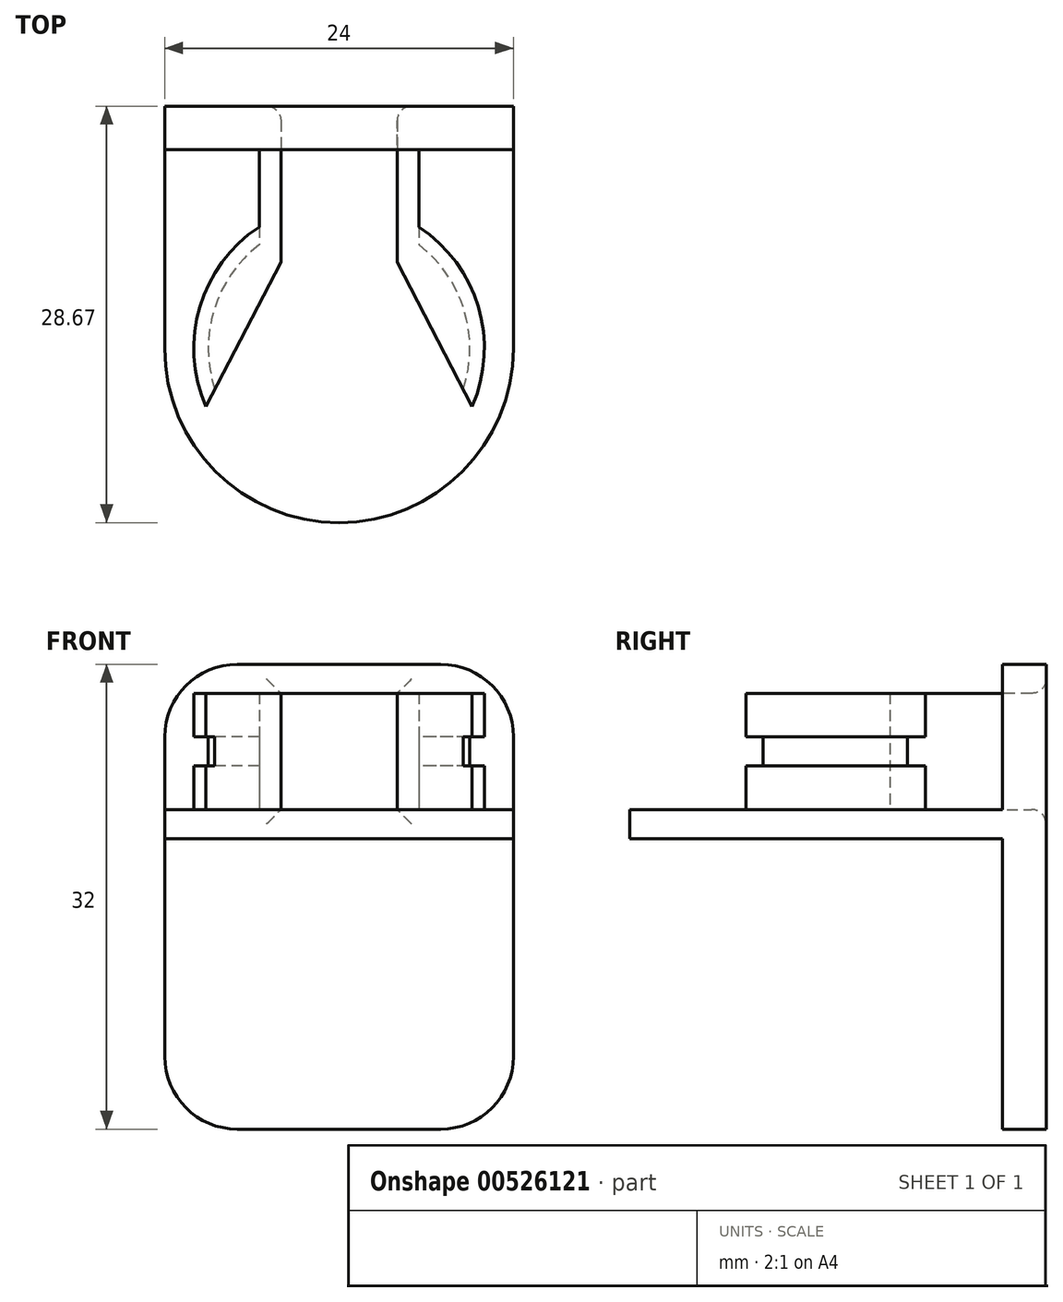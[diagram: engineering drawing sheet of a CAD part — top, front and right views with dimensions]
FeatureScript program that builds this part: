
annotation { "Feature Type Name" : "Feature", "Feature Type Description" : "" }
export const myFeature = defineFeature(function(context is Context, id is Id, definition is map)
    precondition{}
    {
        {
            var Q0;
            Q0=qCreatedBy(makeId("Top.planeOp"),FACE);
            var sketch = newSketch(context, id + "F0", { "sketchPlane" : qUnion([Q0])});
            skArc(sketch, "E0", {"start": v(-5.5, 1.5) * mm, "mid": v(0, 24.17) * mm, "end": v(5.5, 1.5) * mm});
            skArc(sketch, "E1", {"start": v(-5.5, -1.5) * mm, "mid": v(0, -24.17) * mm, "end": v(5.5, -1.5) * mm});
            skLineSegment(sketch, "E2", {"start": v(-5.5, 1.5) * mm, "end": v(-5.5, -1.5) * mm});
            skLineSegment(sketch, "E3", {"start": v(5.5, 1.5) * mm, "end": v(5.5, -1.5) * mm});
            skSolve(sketch);
        }
        {
            var Q0;
            Q0=qSketchRegion(id+"F0",true);
            extrude(context, id + "F1", {"entities" : qUnion([Q0]), "depth" : 2 * mm, "offsetDistance" : 25 * mm});
        }
        {
            var Q0;
            Q0=makeQuery(id+"F1.opExtrude","CAP_FACE",FACE,{"disambiguationData":[OSD([sQuery(id+"F0.wireOp",EDGE,"E0"),sQuery(id+"F0.wireOp",EDGE,"E1"),sQuery(id+"F0.wireOp",EDGE,"E2"),sQuery(id+"F0.wireOp",EDGE,"E3")])],"isStart":false});
            var sketch = newSketch(context, id + "F2", { "sketchPlane" : qUnion([Q0])});
            skArc(sketch, "E4", {"start": v(8.66, 17.17) * mm, "mid": v(9.5, 9.04) * mm, "end": v(4, 3) * mm});
            skArc(sketch, "E5", {"start": v(9.78, 19.11) * mm, "mid": v(11.66, 9.33) * mm, "end": v(5.5, 1.5) * mm});
            skArc(sketch, "E6", {"start": v(-8.66, 17.17) * mm, "mid": v(-9.5, 9.04) * mm, "end": v(-4, 3) * mm});
            skArc(sketch, "E7", {"start": v(5.5, -3.81) * mm, "mid": v(9.59, -9.32) * mm, "end": v(9.17, -16.17) * mm});
            skLineSegment(sketch, "E8", {"start": v(9.78, 19.11) * mm, "end": v(8.66, 17.17) * mm});
            skLineSegment(sketch, "E9", {"start": v(-8.66, 17.17) * mm, "end": v(-9.78, 19.11) * mm});
            skLineSegment(sketch, "E10", {"start": v(5.5, 1.5) * mm, "end": v(5.5, -3.81) * mm});
            skLineSegment(sketch, "E11", {"start": v(-4, 3) * mm, "end": v(-4, -6.24) * mm});
            skLineSegment(sketch, "E12", {"start": v(-4, -6.24) * mm, "end": v(-9.17, -16.17) * mm});
            skLineSegment(sketch, "E13", {"start": v(9.17, -16.17) * mm, "end": v(4, -6.24) * mm});
            skLineSegment(sketch, "E14", {"start": v(4, -6.24) * mm, "end": v(4, 3) * mm});
            skArc(sketch, "E15", {"start": v(-9.78, 19.11) * mm, "mid": v(-11.66, 9.33) * mm, "end": v(-5.5, 1.5) * mm});
            skArc(sketch, "E16", {"start": v(-9.17, -16.17) * mm, "mid": v(-9.59, -9.32) * mm, "end": v(-5.5, -3.81) * mm});
            skLineSegment(sketch, "E17", {"start": v(-5.5, 1.5) * mm, "end": v(-5.5, -3.81) * mm});
            skArc(sketch, "E18.0", {"start": v(-5.5, 1.5) * mm, "mid": v(0, 24.17) * mm, "end": v(5.5, 1.5) * mm, "construction": true});
            skArc(sketch, "E19.0", {"start": v(-5.5, -1.5) * mm, "mid": v(0, -24.17) * mm, "end": v(5.5, -1.5) * mm, "construction": true});
            skSolve(sketch);
        }
        {
            var Q0;
            Q0=qSketchRegion(id+"F2",true);
            extrude(context, id + "F3", {"entities" : qUnion([Q0]), "operationType" : NewBodyOperationType.ADD, "depth" : 3 * mm, "offsetDistance" : 25 * mm});
        }
        {
            var Q0;
            Q0=makeQuery(id+"F3.opExtrude","CAP_FACE",FACE,{"disambiguationData":[OSD([sQuery(id+"F2.wireOp",EDGE,"E4"),sQuery(id+"F2.wireOp",EDGE,"E5"),sQuery(id+"F2.wireOp",EDGE,"E7"),sQuery(id+"F2.wireOp",EDGE,"E8"),sQuery(id+"F2.wireOp",EDGE,"E10"),sQuery(id+"F2.wireOp",EDGE,"E13"),sQuery(id+"F2.wireOp",EDGE,"E14")])],"isStart":false});
            var sketch = newSketch(context, id + "F4", { "sketchPlane" : qUnion([Q0])});
            skArc(sketch, "E20", {"start": v(-9.78, 19.11) * mm, "mid": v(-11.66, 9.33) * mm, "end": v(-5.5, 1.5) * mm});
            skArc(sketch, "E21", {"start": v(9.78, 19.11) * mm, "mid": v(11.66, 9.33) * mm, "end": v(5.5, 1.5) * mm});
            skArc(sketch, "E22", {"start": v(8.07, 16.15) * mm, "mid": v(8.53, 9.28) * mm, "end": v(4, 4.1) * mm});
            skArc(sketch, "E23", {"start": v(-8.07, 16.15) * mm, "mid": v(-8.53, 9.28) * mm, "end": v(-4, 4.1) * mm});
            skArc(sketch, "E24", {"start": v(5.5, -5.04) * mm, "mid": v(8.6, -9.53) * mm, "end": v(8.55, -14.98) * mm});
            skArc(sketch, "E25", {"start": v(-5.5, -5.04) * mm, "mid": v(-8.6, -9.53) * mm, "end": v(-8.55, -14.98) * mm});
            skLineSegment(sketch, "E26", {"start": v(-5.5, 1.5) * mm, "end": v(-5.5, -5.04) * mm});
            skLineSegment(sketch, "E27", {"start": v(5.5, 1.5) * mm, "end": v(5.5, -5.04) * mm});
            skLineSegment(sketch, "E28", {"start": v(-4, 4.1) * mm, "end": v(-4, -6.24) * mm});
            skLineSegment(sketch, "E29", {"start": v(-4, -6.24) * mm, "end": v(-8.55, -14.98) * mm});
            skLineSegment(sketch, "E30", {"start": v(4, 4.1) * mm, "end": v(4, -6.24) * mm});
            skLineSegment(sketch, "E31", {"start": v(4, -6.24) * mm, "end": v(8.55, -14.98) * mm});
            skLineSegment(sketch, "E32", {"start": v(8.07, 16.15) * mm, "end": v(9.78, 19.11) * mm});
            skLineSegment(sketch, "E33", {"start": v(-9.78, 19.11) * mm, "end": v(-8.07, 16.15) * mm});
            skLineSegment(sketch, "E34.0", {"start": v(-8.66, 17.17) * mm, "end": v(-9.78, 19.11) * mm, "construction": true});
            skLineSegment(sketch, "E35.0", {"start": v(9.78, 19.11) * mm, "end": v(8.66, 17.17) * mm, "construction": true});
            skLineSegment(sketch, "E36.0", {"start": v(-4, -6.24) * mm, "end": v(-9.17, -16.17) * mm, "construction": true});
            skLineSegment(sketch, "E37.0", {"start": v(9.17, -16.17) * mm, "end": v(4, -6.24) * mm, "construction": true});
            skArc(sketch, "E38.0", {"start": v(-9.78, 19.11) * mm, "mid": v(0, 24.17) * mm, "end": v(9.78, 19.11) * mm, "construction": true});
            skArc(sketch, "E39.0", {"start": v(-5.5, -1.5) * mm, "mid": v(0, -24.17) * mm, "end": v(5.5, -1.5) * mm, "construction": true});
            skSolve(sketch);
        }
        {
            var Q0;
            Q0=qSketchRegion(id+"F4",true);
            extrude(context, id + "F5", {"entities" : qUnion([Q0]), "operationType" : NewBodyOperationType.ADD, "depth" : 2 * mm, "offsetDistance" : 25 * mm});
        }
        {
            var Q0;
            Q0=makeQuery(id+"F5.opExtrude","CAP_FACE",FACE,{"disambiguationData":[OSD([sQuery(id+"F4.wireOp",EDGE,"E21"),sQuery(id+"F4.wireOp",EDGE,"E22"),sQuery(id+"F4.wireOp",EDGE,"E24"),sQuery(id+"F4.wireOp",EDGE,"E27"),sQuery(id+"F4.wireOp",EDGE,"E30"),sQuery(id+"F4.wireOp",EDGE,"E31"),sQuery(id+"F4.wireOp",EDGE,"E32")])],"isStart":false});
            var sketch = newSketch(context, id + "F6", { "sketchPlane" : qUnion([Q0])});
            skArc(sketch, "E40", {"start": v(8.66, 17.17) * mm, "mid": v(9.5, 9.04) * mm, "end": v(4, 3) * mm});
            skArc(sketch, "E41", {"start": v(9.78, 19.11) * mm, "mid": v(11.66, 9.33) * mm, "end": v(5.5, 1.5) * mm});
            skArc(sketch, "E42", {"start": v(-8.66, 17.17) * mm, "mid": v(-9.5, 9.04) * mm, "end": v(-4, 3) * mm});
            skArc(sketch, "E43", {"start": v(5.5, -3.81) * mm, "mid": v(9.59, -9.32) * mm, "end": v(9.17, -16.17) * mm});
            skLineSegment(sketch, "E44", {"start": v(9.78, 19.11) * mm, "end": v(8.66, 17.17) * mm});
            skLineSegment(sketch, "E45", {"start": v(-8.66, 17.17) * mm, "end": v(-9.78, 19.11) * mm});
            skLineSegment(sketch, "E46", {"start": v(5.5, 1.5) * mm, "end": v(5.5, -3.81) * mm});
            skLineSegment(sketch, "E47", {"start": v(-4, 3) * mm, "end": v(-4, -6.24) * mm});
            skLineSegment(sketch, "E48", {"start": v(-4, -6.24) * mm, "end": v(-9.17, -16.17) * mm});
            skLineSegment(sketch, "E49", {"start": v(9.17, -16.17) * mm, "end": v(4, -6.24) * mm});
            skLineSegment(sketch, "E50", {"start": v(4, -6.24) * mm, "end": v(4, 3) * mm});
            skArc(sketch, "E51", {"start": v(-9.78, 19.11) * mm, "mid": v(-11.66, 9.33) * mm, "end": v(-5.5, 1.5) * mm});
            skArc(sketch, "E52", {"start": v(-9.17, -16.17) * mm, "mid": v(-9.59, -9.32) * mm, "end": v(-5.5, -3.81) * mm});
            skLineSegment(sketch, "E53", {"start": v(-5.5, 1.5) * mm, "end": v(-5.5, -3.81) * mm});
            skArc(sketch, "E54.0", {"start": v(-5.5, -1.5) * mm, "mid": v(0, -24.17) * mm, "end": v(5.5, -1.5) * mm, "construction": true});
            skArc(sketch, "E55.0", {"start": v(-9.78, 19.11) * mm, "mid": v(0, 24.17) * mm, "end": v(9.78, 19.11) * mm, "construction": true});
            skSolve(sketch);
        }
        {
            var Q0;
            Q0=qSketchRegion(id+"F6",true);
            extrude(context, id + "F7", {"entities" : qUnion([Q0]), "operationType" : NewBodyOperationType.ADD, "depth" : 3 * mm, "offsetDistance" : 25 * mm});
        }
        {
            var Q0;
            Q0=makeQuery(id+"F5.opExtrude","CAP_EDGE",EDGE,{"disambiguationData":[OSD([sQuery(id+"F4.wireOp",EDGE,"E22")])],"isStart":false});
            var Q1;
            Q1=makeQuery(id+"F5.opExtrude","CAP_EDGE",EDGE,{"disambiguationData":[OSD([sQuery(id+"F4.wireOp",EDGE,"E23")])],"isStart":false});
            var Q2;
            Q2=makeQuery(id+"F5.opExtrude","CAP_EDGE",EDGE,{"disambiguationData":[OSD([sQuery(id+"F4.wireOp",EDGE,"E23")])],"isStart":true});
            var Q3;
            Q3=makeQuery(id+"F5.opExtrude","CAP_EDGE",EDGE,{"disambiguationData":[OSD([sQuery(id+"F4.wireOp",EDGE,"E22")])],"isStart":true});
            var Q4;
            Q4=makeQuery(id+"F5.opExtrude","CAP_EDGE",EDGE,{"disambiguationData":[OSD([sQuery(id+"F4.wireOp",EDGE,"E25")])],"isStart":true});
            var Q5;
            Q5=makeQuery(id+"F5.opExtrude","CAP_EDGE",EDGE,{"disambiguationData":[OSD([sQuery(id+"F4.wireOp",EDGE,"E25")])],"isStart":false});
            var Q6;
            Q6=makeQuery(id+"F5.opExtrude","CAP_EDGE",EDGE,{"disambiguationData":[OSD([sQuery(id+"F4.wireOp",EDGE,"E24")])],"isStart":false});
            var Q7;
            Q7=makeQuery(id+"F5.opExtrude","CAP_EDGE",EDGE,{"disambiguationData":[OSD([sQuery(id+"F4.wireOp",EDGE,"E24")])],"isStart":true});
            fillet(context, id + "F8", {"entities" : qUnion([Q0, Q1, Q2, Q3, Q4, Q5, Q6, Q7]), "radius" : 1 * mm, "tangentPropagation" : true, "allowEdgeOverflow" : false});
        }
        {
            var Q0;
            Q0=makeQuery(id+"F7.opExtrude","CAP_FACE",FACE,{"disambiguationData":[OSD([sQuery(id+"F6.wireOp",EDGE,"E40"),sQuery(id+"F6.wireOp",EDGE,"E41"),sQuery(id+"F6.wireOp",EDGE,"E43"),sQuery(id+"F6.wireOp",EDGE,"E44"),sQuery(id+"F6.wireOp",EDGE,"E46"),sQuery(id+"F6.wireOp",EDGE,"E49"),sQuery(id+"F6.wireOp",EDGE,"E50")])],"isStart":false});
            var sketch = newSketch(context, id + "F9", { "sketchPlane" : qUnion([Q0])});
            skLineSegment(sketch, "E56.bottom", {"start": v(-12, 1.5) * mm, "end": v(12, 1.5) * mm});
            skLineSegment(sketch, "E56.top", {"start": v(-12, 24.17) * mm, "end": v(12, 24.17) * mm});
            skLineSegment(sketch, "E56.left", {"start": v(-12, 24.17) * mm, "end": v(-12, 1.5) * mm});
            skLineSegment(sketch, "E56.right", {"start": v(12, 24.17) * mm, "end": v(12, 1.5) * mm});
            skSolve(sketch);
        }
        {
            var Q0;
            Q0=qSketchRegion(id+"F9",true);
            extrude(context, id + "F10", {"entities" : qUnion([Q0]), "operationType" : NewBodyOperationType.REMOVE, "oppositeDirection" : true, "depth" : 10 * mm, "offsetDistance" : 25 * mm});
        }
        {
            var Q0;
            Q0=makeQuery(id+"F10.boolean.opBoolean","COPY",FACE,{"derivedFrom":makeQuery(id+"F10.opExtrude","SWEPT_FACE",FACE,{"disambiguationData":[OSD([sQuery(id+"F9.wireOp",EDGE,"E56.bottom")])]})});
            var sketch = newSketch(context, id + "F11", { "sketchPlane" : qUnion([Q0])});
            skLineSegment(sketch, "E57.bottom", {"start": v(-12, -20) * mm, "end": v(12, -20) * mm});
            skLineSegment(sketch, "E57.top", {"start": v(-12, 12) * mm, "end": v(12, 12) * mm});
            skLineSegment(sketch, "E57.left", {"start": v(-12, 12) * mm, "end": v(-12, -20) * mm});
            skLineSegment(sketch, "E57.right", {"start": v(12, 12) * mm, "end": v(12, -20) * mm});
            skLineSegment(sketch, "E58.bottom", {"start": v(-4, 10) * mm, "end": v(4, 10) * mm});
            skLineSegment(sketch, "E58.top", {"start": v(-4, 2) * mm, "end": v(4, 2) * mm});
            skLineSegment(sketch, "E58.left", {"start": v(4, 10) * mm, "end": v(4, 2) * mm});
            skLineSegment(sketch, "E58.right", {"start": v(-4, 10) * mm, "end": v(-4, 2) * mm});
            skSolve(sketch);
        }
        {
            var Q0;
            Q0=qSketchRegion(id+"F11",true);
            extrude(context, id + "F12", {"entities" : qUnion([Q0]), "operationType" : NewBodyOperationType.ADD, "depth" : 3 * mm, "offsetDistance" : 25 * mm});
        }
        {
            var Q0;
            Q0=makeQuery(id+"F12.opExtrude","CAP_EDGE",EDGE,{"disambiguationData":[OSD([sQuery(id+"F11.wireOp",EDGE,"E58.bottom")])],"isStart":false});
            var Q1;
            Q1=makeQuery(id+"F12.opExtrude","CAP_EDGE",EDGE,{"disambiguationData":[OSD([sQuery(id+"F11.wireOp",EDGE,"E58.right")])],"isStart":false});
            var Q2;
            Q2=makeQuery(id+"F12.opExtrude","CAP_EDGE",EDGE,{"disambiguationData":[OSD([sQuery(id+"F11.wireOp",EDGE,"E58.left")])],"isStart":false});
            var Q3;
            Q3=makeQuery(id+"F12.opExtrude","CAP_EDGE",EDGE,{"disambiguationData":[OSD([sQuery(id+"F11.wireOp",EDGE,"E58.top")])],"isStart":false});
            fillet(context, id + "F13", {"entities" : qUnion([Q0, Q1, Q2, Q3]), "radius" : 1 * mm, "tangentPropagation" : true, "allowEdgeOverflow" : false});
        }
        {
            var Q0;
            Q0=makeQuery(id+"F12.opExtrude","SWEPT_EDGE",EDGE,{"disambiguationData":[OSD([sQuery(id+"F11.wireOp",EDGE,"E57.top"),sQuery(id+"F11.wireOp",EDGE,"E57.left")])]});
            var Q1;
            Q1=makeQuery(id+"F12.opExtrude","SWEPT_EDGE",EDGE,{"disambiguationData":[OSD([sQuery(id+"F11.wireOp",EDGE,"E57.top"),sQuery(id+"F11.wireOp",EDGE,"E57.right")])]});
            var Q2;
            Q2=makeQuery(id+"F12.opExtrude","SWEPT_EDGE",EDGE,{"disambiguationData":[OSD([sQuery(id+"F11.wireOp",EDGE,"E57.bottom"),sQuery(id+"F11.wireOp",EDGE,"E57.right")])]});
            var Q3;
            Q3=makeQuery(id+"F12.opExtrude","SWEPT_EDGE",EDGE,{"disambiguationData":[OSD([sQuery(id+"F11.wireOp",EDGE,"E57.bottom"),sQuery(id+"F11.wireOp",EDGE,"E57.left")])]});
            fillet(context, id + "F14", {"entities" : qUnion([Q0, Q1, Q2, Q3]), "radius" : 5 * mm, "tangentPropagation" : true, "allowEdgeOverflow" : false});
        }
        {
            var Q0;
            Q0=makeQuery(id+"F1.opExtrude","CAP_FACE",FACE,{"disambiguationData":[OSD([sQuery(id+"F0.wireOp",EDGE,"E0"),sQuery(id+"F0.wireOp",EDGE,"E1"),sQuery(id+"F0.wireOp",EDGE,"E2"),sQuery(id+"F0.wireOp",EDGE,"E3")])],"isStart":true});
            var sketch = newSketch(context, id + "F15", { "sketchPlane" : qUnion([Q0])});
            skLineSegment(sketch, "E59.bottom", {"start": v(-12, -1.5) * mm, "end": v(12, -1.5) * mm});
            skLineSegment(sketch, "E59.top", {"start": v(-12, 12.17) * mm, "end": v(12, 12.17) * mm});
            skLineSegment(sketch, "E59.left", {"start": v(-12, 12.17) * mm, "end": v(-12, -1.5) * mm});
            skLineSegment(sketch, "E59.right", {"start": v(12, 12.17) * mm, "end": v(12, -1.5) * mm});
            skSolve(sketch);
        }
        {
            var Q0;
            Q0=qSketchRegion(id+"F15",true);
            extrude(context, id + "F16", {"entities" : qUnion([Q0]), "operationType" : NewBodyOperationType.ADD, "oppositeDirection" : true, "depth" : 2 * mm, "offsetDistance" : 25 * mm});
        }
    });
